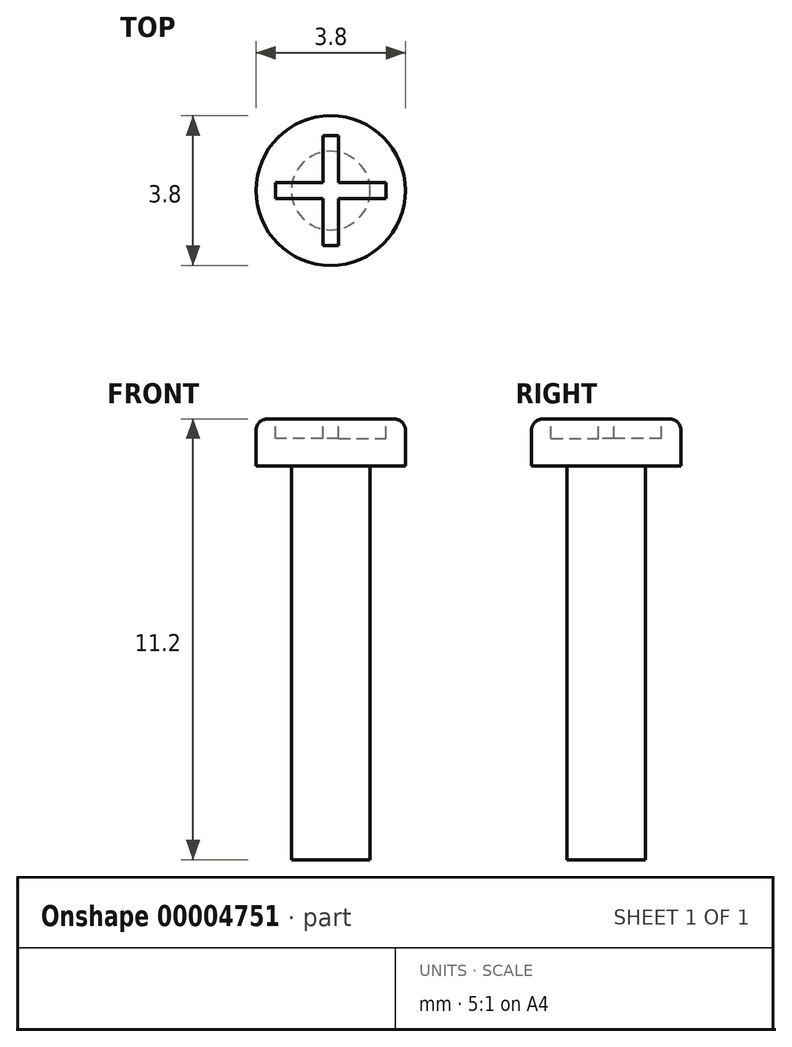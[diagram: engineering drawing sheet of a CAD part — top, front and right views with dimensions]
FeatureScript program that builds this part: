
annotation { "Feature Type Name" : "Feature", "Feature Type Description" : "" }
export const myFeature = defineFeature(function(context is Context, id is Id, definition is map)
    precondition{}
    {
        {
            var Q0;
            Q0=qCreatedBy(makeId("Top.planeOp"),FACE);
            var sketch = newSketch(context, id + "F0", { "sketchPlane" : qUnion([Q0])});
            skCircle(sketch, "E0", {"center": v(0, 0) * mm, "radius": 1.9 * mm});
            skSolve(sketch);
        }
        {
            var Q0;
            Q0=makeQuery(id+"F0.imprint","IMPRINT",FACE,{"disambiguationData":[TD([[makeQuery(id+"F0.imprint","IMPRINT",EDGE,{"derivedFrom":sQuery(id+"F0.wireOp",EDGE,"E0")}),1.0]])]});
            extrude(context, id + "F1", {"entities" : qUnion([Q0]), "depth" : 1.2 * mm});
        }
        {
            var Q0;
            Q0=makeQuery(id+"F1.opExtrude","CAP_FACE",FACE,{"disambiguationData":[OSD([sQuery(id+"F0.wireOp",EDGE,"E0")])],"isStart":false});
            var sketch = newSketch(context, id + "F2", { "sketchPlane" : qUnion([Q0])});
            skCircle(sketch, "E1.0", {"center": v(0, 0) * mm, "radius": 1.9 * mm, "construction": true});
            skLineSegment(sketch, "E2", {"start": v(0, 0) * mm, "end": v(1.9, 0) * mm, "construction": true});
            skLineSegment(sketch, "E3", {"start": v(0, 0) * mm, "end": v(0, 1.9) * mm, "construction": true});
            skLineSegment(sketch, "E4", {"start": v(0, 1.4) * mm, "end": v(0.2, 1.4) * mm});
            skLineSegment(sketch, "E5", {"start": v(0.2, 1.4) * mm, "end": v(0.2, 0.2) * mm});
            skLineSegment(sketch, "E6", {"start": v(0.2, 0.2) * mm, "end": v(1.4, 0.2) * mm});
            skLineSegment(sketch, "E7", {"start": v(1.4, 0.2) * mm, "end": v(1.4, 0) * mm});
            skLineSegment(sketch, "E8.0.MirrorCS", {"start": v(0, 1.4) * mm, "end": v(-0.2, 1.4) * mm});
            skLineSegment(sketch, "E9.0.MirrorCS", {"start": v(-0.2, 1.4) * mm, "end": v(-0.2, 0.2) * mm});
            skLineSegment(sketch, "E10.0.MirrorCS", {"start": v(-0.2, 0.2) * mm, "end": v(-1.4, 0.2) * mm});
            skLineSegment(sketch, "E11.0.MirrorCS", {"start": v(-1.4, 0.2) * mm, "end": v(-1.4, 0) * mm});
            skLineSegment(sketch, "E12.0.MirrorCS", {"start": v(1.4, -0.2) * mm, "end": v(1.4, 0) * mm});
            skLineSegment(sketch, "E13.0.MirrorCS", {"start": v(0.2, -0.2) * mm, "end": v(1.4, -0.2) * mm});
            skLineSegment(sketch, "E14.0.MirrorCS", {"start": v(0.2, -1.4) * mm, "end": v(0.2, -0.2) * mm});
            skLineSegment(sketch, "E15.0.MirrorCS", {"start": v(-0.2, -1.4) * mm, "end": v(-0.2, -0.2) * mm});
            skLineSegment(sketch, "E16.0.MirrorCS", {"start": v(-0.2, -0.2) * mm, "end": v(-1.4, -0.2) * mm});
            skLineSegment(sketch, "E17.0.MirrorCS", {"start": v(-1.4, -0.2) * mm, "end": v(-1.4, 0) * mm});
            skLineSegment(sketch, "E18.0.MirrorCS", {"start": v(0, -1.4) * mm, "end": v(-0.2, -1.4) * mm});
            skLineSegment(sketch, "E19.0.MirrorCS", {"start": v(0, -1.4) * mm, "end": v(0.2, -1.4) * mm});
            skSolve(sketch);
        }
        {
            var Q0;
            Q0=makeQuery(id+"F2.imprint","IMPRINT",FACE,{"disambiguationData":[TD([[makeQuery(id+"F2.imprint","IMPRINT",EDGE,{"derivedFrom":sQuery(id+"F2.wireOp",EDGE,"E4")}),-1.0]])]});
            extrude(context, id + "F3", {"entities" : qUnion([Q0]), "operationType" : NewBodyOperationType.REMOVE, "oppositeDirection" : true, "depth" : 0.5 * mm});
        }
        {
            var Q0;
            Q0=makeQuery(id+"F1.opExtrude","CAP_EDGE",EDGE,{"disambiguationData":[OSD([sQuery(id+"F0.wireOp",EDGE,"E0")])],"isStart":false});
            fillet(context, id + "F4", {"entities" : qUnion([Q0]), "radius" : 0.3 * mm, "tangentPropagation" : true, "allowEdgeOverflow" : false});
        }
        {
            var Q0;
            Q0=makeQuery(id+"F1.opExtrude","CAP_FACE",FACE,{"disambiguationData":[OSD([sQuery(id+"F0.wireOp",EDGE,"E0")])],"isStart":true});
            var sketch = newSketch(context, id + "F5", { "sketchPlane" : qUnion([Q0])});
            skCircle(sketch, "E20.0", {"center": v(0, 0) * mm, "radius": 1.9 * mm, "construction": true});
            skCircle(sketch, "E21", {"center": v(0, 0) * mm, "radius": 1 * mm});
            skSolve(sketch);
        }
        {
            var Q0;
            Q0=makeQuery(id+"F5.imprint","IMPRINT",FACE,{"disambiguationData":[TD([[makeQuery(id+"F5.imprint","IMPRINT",EDGE,{"derivedFrom":sQuery(id+"F5.wireOp",EDGE,"E21")}),1.0]])]});
            extrude(context, id + "F6", {"entities" : qUnion([Q0]), "operationType" : NewBodyOperationType.ADD, "depth" : 10 * mm});
        }
    });
